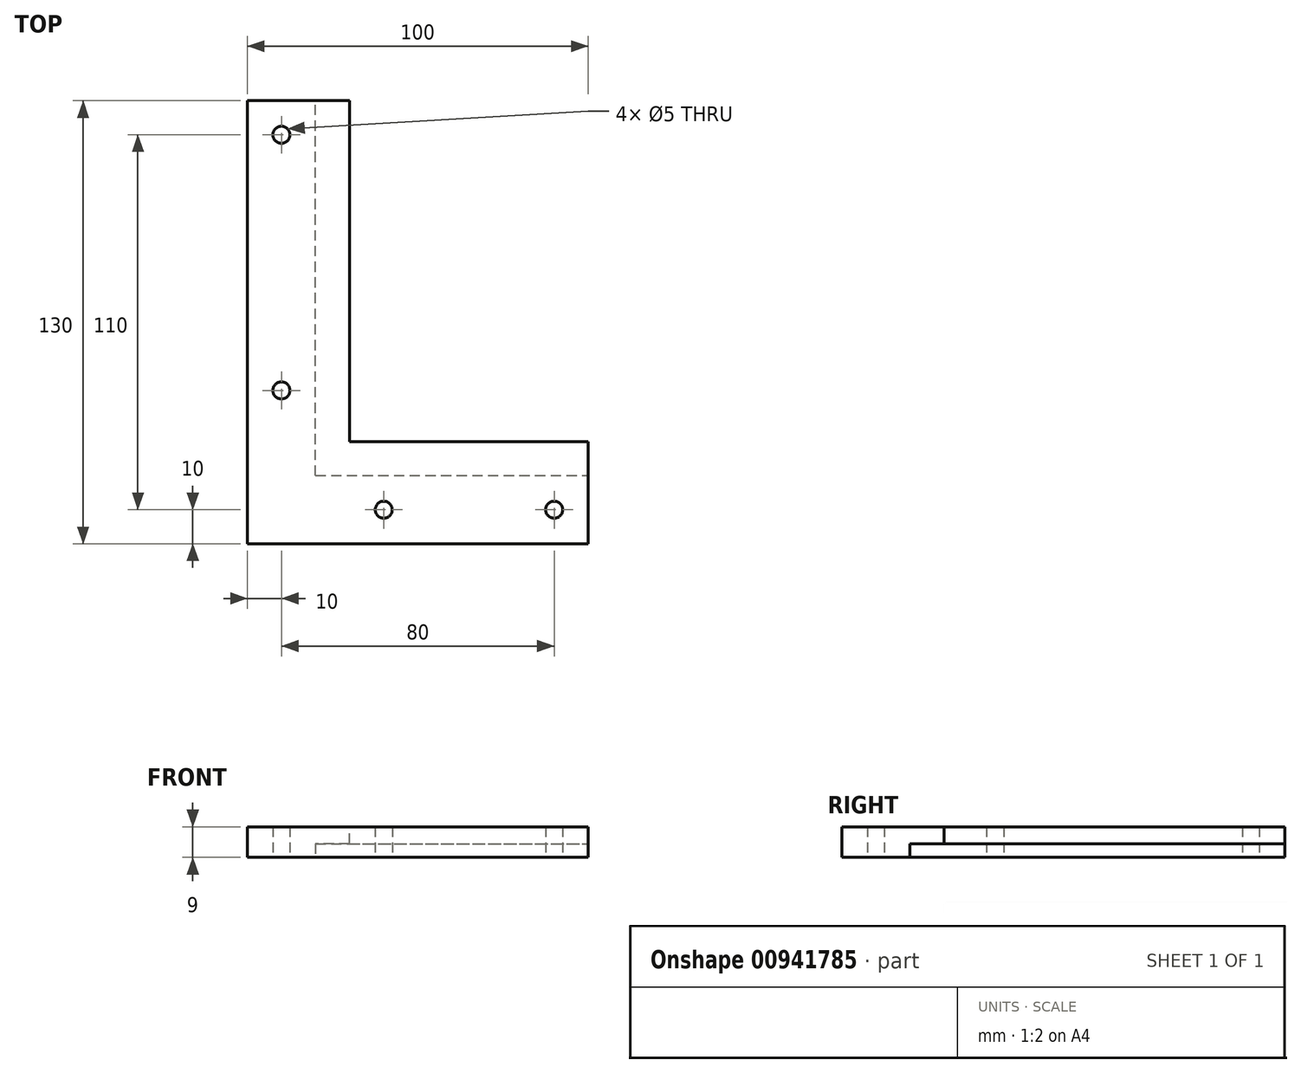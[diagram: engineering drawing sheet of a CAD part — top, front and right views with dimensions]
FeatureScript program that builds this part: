
annotation { "Feature Type Name" : "Feature", "Feature Type Description" : "" }
export const myFeature = defineFeature(function(context is Context, id is Id, definition is map)
    precondition{}
    {
        {
            var Q0;
            Q0=qCreatedBy(makeId("Top.planeOp"),FACE);
            var sketch = newSketch(context, id + "F0", { "sketchPlane" : qUnion([Q0])});
            skEllipticalArc(sketch, "E0", {});
            skLineSegment(sketch, "E1", {"start": v(-86.5, 0) * mm, "end": v(-86.5, -116.5) * mm});
            skPoint(sketch, "E1.endSnap0", {"position": v(0, -116.5) * mm});
            skLineSegment(sketch, "E2", {"start": v(-86.5, -116.5) * mm, "end": v(0, -116.5) * mm});
            skLineSegment(sketch, "E3", {"start": v(-86.5, 0) * mm, "end": v(-100, 0) * mm});
            skLineSegment(sketch, "E4", {"start": v(-100, 0) * mm, "end": v(-100, -130) * mm});
            skLineSegment(sketch, "E5", {"start": v(-100, -130) * mm, "end": v(0, -130) * mm});
            skLineSegment(sketch, "E6", {"start": v(0, -130) * mm, "end": v(0, -116.5) * mm});
            const initialGuessF0  = {"E0": [0, 0, 1, 0, 0.0865, 0.1165, 3.141592653589793, 4.71238898038469]};
            skSetInitialGuess(sketch, initialGuessF0);
            skSolve(sketch);
        }
        {
            var Q0;
            Q0=qSketchRegion(id+"F0",true);
            extrude(context, id + "F1", {"entities" : qUnion([Q0]), "depth" : 12 * mm, "offsetDistance" : 25 * mm});
        }
        {
            var Q0;
            Q0=makeQuery(id+"F1.opExtrude","SWEPT_FACE",FACE,{"disambiguationData":[OSD([sQuery(id+"F0.wireOp",EDGE,"E5")])]});
            var sketch = newSketch(context, id + "F2", { "sketchPlane" : qUnion([Q0])});
            skLineSegment(sketch, "E7.bottom", {"start": v(-100, 16) * mm, "end": v(0, 16) * mm});
            skLineSegment(sketch, "E7.top", {"start": v(-100, -4) * mm, "end": v(0, -4) * mm});
            skLineSegment(sketch, "E7.left", {"start": v(-100, 16) * mm, "end": v(-100, -4) * mm});
            skLineSegment(sketch, "E7.right", {"start": v(0, 16) * mm, "end": v(0, -4) * mm});
            skSolve(sketch);
        }
        {
            var Q0;
            Q0=qSketchRegion(id+"F2",true);
            extrude(context, id + "F3", {"entities" : qUnion([Q0]), "operationType" : NewBodyOperationType.ADD, "depth" : 5 * mm, "offsetDistance" : 25 * mm});
        }
        {
            var Q0;
            Q0=makeQuery(id+"F3.boolean.opBoolean","MERGE",FACE,{"derivedFrom":[makeQuery(id+"F1.opExtrude","SWEPT_FACE",FACE,{"disambiguationData":[OSD([sQuery(id+"F0.wireOp",EDGE,"E4")])]}),makeQuery(id+"F3.opExtrude","SWEPT_FACE",FACE,{"disambiguationData":[OSD([sQuery(id+"F2.wireOp",EDGE,"E7.left")])]})]});
            var sketch = newSketch(context, id + "F4", { "sketchPlane" : qUnion([Q0])});
            skLineSegment(sketch, "E8.bottom", {"start": v(135, 16) * mm, "end": v(0, 16) * mm});
            skLineSegment(sketch, "E8.top", {"start": v(135, -4) * mm, "end": v(0, -4) * mm});
            skLineSegment(sketch, "E8.left", {"start": v(135, 16) * mm, "end": v(135, -4) * mm});
            skLineSegment(sketch, "E8.right", {"start": v(0, 16) * mm, "end": v(0, -4) * mm});
            skSolve(sketch);
        }
        {
            var Q0;
            Q0=qSketchRegion(id+"F4",true);
            extrude(context, id + "F5", {"entities" : qUnion([Q0]), "operationType" : NewBodyOperationType.ADD, "depth" : 5 * mm, "offsetDistance" : 25 * mm});
        }
        {
            var Q0;
            Q0=makeQuery(id+"F5.boolean.opBoolean","MERGE",FACE,{"derivedFrom":[makeQuery(id+"F3.opExtrude","SWEPT_FACE",FACE,{"disambiguationData":[OSD([sQuery(id+"F2.wireOp",EDGE,"E7.bottom")])]}),makeQuery(id+"F5.opExtrude","SWEPT_FACE",FACE,{"disambiguationData":[OSD([sQuery(id+"F4.wireOp",EDGE,"E8.bottom")])]})]});
            var sketch = newSketch(context, id + "F6", { "sketchPlane" : qUnion([Q0])});
            skLineSegment(sketch, "E9", {"start": v(-105, 0) * mm, "end": v(-90, 0) * mm});
            skLineSegment(sketch, "E10", {"start": v(-90, 0) * mm, "end": v(-90, -120) * mm});
            skLineSegment(sketch, "E11", {"start": v(-90, -120) * mm, "end": v(0, -120) * mm});
            skLineSegment(sketch, "E12", {"start": v(0, -120) * mm, "end": v(0, -135) * mm});
            skLineSegment(sketch, "E13", {"start": v(0, -135) * mm, "end": v(-105, -135) * mm});
            skLineSegment(sketch, "E14", {"start": v(-105, -135) * mm, "end": v(-105, 0) * mm});
            skSolve(sketch);
        }
        {
            var Q0;
            Q0=makeQuery(id+"F5.boolean.opBoolean","MERGE",FACE,{"derivedFrom":[makeQuery(id+"F3.opExtrude","SWEPT_FACE",FACE,{"disambiguationData":[OSD([sQuery(id+"F2.wireOp",EDGE,"E7.top")])]}),makeQuery(id+"F5.opExtrude","SWEPT_FACE",FACE,{"disambiguationData":[OSD([sQuery(id+"F4.wireOp",EDGE,"E8.top")])]})]});
            var sketch = newSketch(context, id + "F7", { "sketchPlane" : qUnion([Q0])});
            skLineSegment(sketch, "E15", {"start": v(0, 150) * mm, "end": v(-120, 150) * mm});
            skLineSegment(sketch, "E16", {"start": v(-120, 150) * mm, "end": v(-120, 0) * mm});
            skLineSegment(sketch, "E17", {"start": v(-120, 0) * mm, "end": v(-105, 0) * mm});
            skLineSegment(sketch, "E18", {"start": v(-105, 0) * mm, "end": v(-105, 135) * mm});
            skLineSegment(sketch, "E19", {"start": v(-105, 135) * mm, "end": v(0, 135) * mm});
            skLineSegment(sketch, "E20", {"start": v(0, 135) * mm, "end": v(0, 150) * mm});
            skCircle(sketch, "E21", {"center": v(-110, 30) * mm, "radius": 2.5 * mm});
            skCircle(sketch, "E22", {"center": v(-110, 105) * mm, "radius": 2.5 * mm});
            skCircle(sketch, "E23", {"center": v(-80, 140) * mm, "radius": 2.5 * mm});
            skCircle(sketch, "E24", {"center": v(-30, 140) * mm, "radius": 2.5 * mm});
            skSolve(sketch);
        }
        {
            var Q0;
            Q0=qSketchRegion(id+"F7",true);
            extrude(context, id + "F8", {"entities" : qUnion([Q0]), "operationType" : NewBodyOperationType.ADD, "oppositeDirection" : true, "depth" : 25 * mm, "offsetDistance" : 25 * mm});
        }
        {
            var Q0;
            Q0=qSketchRegion(id+"F6",true);
            extrude(context, id + "F9", {"entities" : qUnion([Q0]), "operationType" : NewBodyOperationType.ADD, "depth" : 5 * mm, "offsetDistance" : 25 * mm});
        }
        {
            var Q0;
            Q0=qCreatedBy(makeId("Top.planeOp"),FACE);
            var sketch = newSketch(context, id + "F10", { "sketchPlane" : qUnion([Q0])});
            skLineSegment(sketch, "E25.bottom", {"start": v(0, 0) * mm, "end": v(-120, 0) * mm});
            skLineSegment(sketch, "E25.top", {"start": v(0, -20) * mm, "end": v(-120, -20) * mm});
            skLineSegment(sketch, "E25.left", {"start": v(0, 0) * mm, "end": v(0, -20) * mm});
            skLineSegment(sketch, "E25.right", {"start": v(-120, 0) * mm, "end": v(-120, -20) * mm});
            skLineSegment(sketch, "E26.bottom", {"start": v(0, 0) * mm, "end": v(-20, 0) * mm});
            skLineSegment(sketch, "E26.top", {"start": v(0, -150) * mm, "end": v(-20, -150) * mm});
            skLineSegment(sketch, "E26.left", {"start": v(0, 0) * mm, "end": v(0, -150) * mm});
            skLineSegment(sketch, "E26.right", {"start": v(-20, 0) * mm, "end": v(-20, -150) * mm});
            skSolve(sketch);
        }
        {
            var Q0;
            Q0=qSketchRegion(id+"F10",true);
            extrude(context, id + "F11", {"entities" : qUnion([Q0]), "operationType" : NewBodyOperationType.REMOVE, "endBound" : BoundingType.SYMMETRIC, "oppositeDirection" : true, "depth" : 50 * mm, "offsetDistance" : 25 * mm});
        }
        {
            var Q0;
            Q0=makeQuery(id+"F11.boolean.opBoolean","COPY",FACE,{"derivedFrom":makeQuery(id+"F11.opExtrude","SWEPT_FACE",FACE,{"disambiguationData":[OSD([sQuery(id+"F10.wireOp",EDGE,"E26.right")])]})});
            var sketch = newSketch(context, id + "F12", { "sketchPlane" : qUnion([Q0])});
            skLineSegment(sketch, "E27.bottom", {"start": v(-150, -4) * mm, "end": v(-20, -4) * mm});
            skLineSegment(sketch, "E27.top", {"start": v(-150, 12) * mm, "end": v(-20, 12) * mm});
            skLineSegment(sketch, "E27.left", {"start": v(-150, -4) * mm, "end": v(-150, 12) * mm});
            skLineSegment(sketch, "E27.right", {"start": v(-20, -4) * mm, "end": v(-20, 12) * mm});
            skSolve(sketch);
        }
        {
            var Q0;
            Q0 = qSketchRegion(id + "F12", true);
            extrude(context, id + "F13", {"entities" : qUnion([Q0]), "operationType" : NewBodyOperationType.REMOVE, "endBound" : BoundingType.THROUGH_ALL, "oppositeDirection" : true, "depth" : 25 * mm, "offsetDistance" : 25 * mm});
        }
    });
